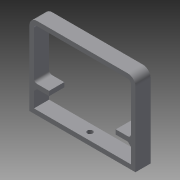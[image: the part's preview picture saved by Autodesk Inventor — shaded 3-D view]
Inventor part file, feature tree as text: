
AUTODESK INVENTOR PART (.ipt)
format: ipt  version: 2014 SP2 (Build 180246200, 246)  size: 122,368 bytes
history: native  units: mm
features: extrude x2, sketch x2
ambient origin geometry x8: Origin, YZ Plane, XZ Plane, XY Plane, X Axis, Y Axis, Z Axis, Center Point
bodies: Solid1 (feature_tree)
feature tree (4):
  extrude  "Extrusion1"  Depth=33.0mm
  extrude  "Extrusion2"  Depth=10.0mm
  sketch  "Sketch1"  dims[d0=64.0mm d1=33.0mm]
  sketch  "Sketch2"  dims[d2=32.0mm d3=16.5mm d4=2.0mm d5=3.0mm d6=70.0mm d9=10.0mm d10=10.0mm d11=20.0mm d12=3.0mm d13=2.0mm d14=2.0mm d15=2.0mm d16=2.0mm d17=10.0mm d18=0.0mm d19=3.5mm d20=10.0mm d21=0.0mm]
